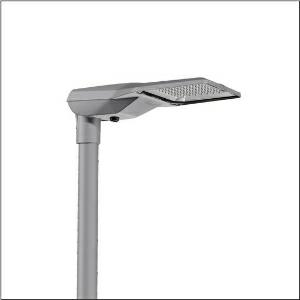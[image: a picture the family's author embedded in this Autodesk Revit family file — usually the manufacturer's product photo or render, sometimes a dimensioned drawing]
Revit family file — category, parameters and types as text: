
# Revit family: streetlight_sl_21_midi___p0_8a_5xe3u33r08lb_5b19
name_source: partatom
category: Lighting Fixtures
units: mm (PartAtom-declared; Revit-internal decimal feet)

## family parameters
Cut with Voids When Loaded = No
Host = Face
Light Source = No
Part Type = Normal
Room Calculation Point = No
Round Connector Dimension = Use Diameter
Shared = No

## types (1)
- --- (1 x LED, 14470 lm, 99.6 W, 3000K)
    Apparent Load = 100 VA
    CIE Flux Codes = 33 69 96 100 100
    Color Rendering = 70
    Color Temperature = 3000K
    Default Elevation = 1800 mm
    Description = Streetlight SL 21 midi, mast luminaire, primary light control with lens, of PMMA, primary optical cover: cover, of toughened safety glass, transparent, light distribution: P0.8a, light emission: direct distribution, primary light characteristic: asymmetric, installation type: post-top, side-entry, LED, High Power LED, rated luminous flux: 14.470lm, luminous efficacy: 145lm/W, light colour: 730, colour temperature: 3000K, control gear: D4i, control: pre-setting: logarithmic dimming characteristic, flexible luminous flux parameterisation, time-dependent luminous flux control, constant luminous flux control, overheat protection, mains connection: 230..240V, AC, 50/60Hz, start of lifetime: 100W, end of service life: 102W, reduction: 46W, luminaire housing, of diecast aluminium, powder-coated, SITECO metallic grey (DB 702S), corrosivity category C5 high according to DIN EN ISO 12944, multi-level sealing system, sealing non-destructively replaceable, inclination adjustable: 0°, 5°, 10°, 15°, please order mast flange separately, length: 644mm, width: 335mm, height: 110mm, mast flange for spigot size: 42mm (side-entry): 5XC10008XM4, 60/48mm (side-entry/post-top): 5XC10108XM2, 76/60mm (side-entry/post-top): 5XC10108XM1, mounting height: 4..8m, Smart Interface below, protection rating (complete): IP66, insulation class (complete): insulation class II (safety insulation), certification: CE, ENEC, ENEC+, VDE, impact resistance: IK10, permissible operating ambient temperature for outdoor applications: -40..+50°C, standard-compliant lighting for roads and squares, packaging unit: 1 piece

Light Distribution: P0.8a
    Height = 111 mm
    Lamp = 1 x LED
    Lamp Light Flux = 14470 lm
    Lamp Power = 99.6 W
    Lamp count = 1
    Length = 644 mm
    Luminous efficacy = 145 lm/W
    Manufacturer = Siteco
    ModVariant = No
    Model = 5XE3U33R08LB
    Number of Poles = 1
    OnlyDefault = Yes
    Power Factor = 1
    Product Name = Streetlight SL 21 midi | P0.8a
    Product group = mast luminaire | pylon top
    ProductGroupID = 6100
    Protection Class = Protection class II
    Protection Degree = IP 66
    RLX_Detail_Level = 1
    RLX_Emergency_Light_Flux = 0 lm
    RLX_Emergency_Type = 0
    RLX_Emergency_Type_DB = No
    RlxData = <blob elided: 26737 chars, md5=bc6cf9b7>
    Socket = socket
    Standby Power = 0 W
    System Light Flux = 14470 lm
    System Power = 100 W
    Type Comments = factory setting: luminous flux: 100 % | dim-lin: 254 | 1020 mA
    Type Image = l_1004300.jpg
    URL = http://relux.com
    VarID = @adj_033229
    Voltage = 0 V
    Weight = 0.00 kg
    Width = 336 mm

## geometry (parser evidence)
native form markers: Blend x4, Sweep x10
no freeform markers — native parametric forms only
